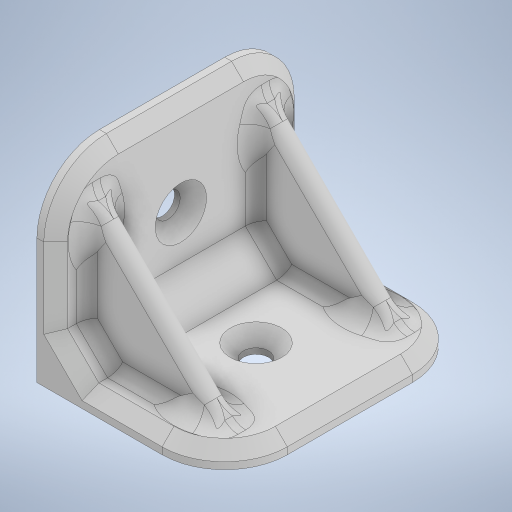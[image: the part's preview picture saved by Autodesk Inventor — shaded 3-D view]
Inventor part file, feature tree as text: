
AUTODESK INVENTOR PART (.ipt)
format: ipt  version: 2024.1 (Build 281209000, 209)  size: 785,920 bytes
history: native  units: in
note: dims shown in document units (in); Inventor stores cm internally (conversion verified against a paired STEP export)
features: sketch x7, extrude x5, fillet x4, plane x2, chamfer x2, hole x2, other x1, mirror x1, projected_geometry x1
ambient origin geometry x8: Origin, YZ Plane, XZ Plane, XY Plane, X Axis, Y Axis, Z Axis, Center Point
bodies: Body1 (feature_tree)
feature tree (25):
  other  "bracket"
  extrude  "Extrusion1"  Depth=1.1811in
  extrude  "Extrusion2"  Depth=0.1181in
  extrude  "Extrusion3"  Depth=0.1575in
  extrude  "Extrusion4"  Depth=0.7874in
  plane  "Work Plane1"
  extrude  "Extrusion5"  Depth=0.5906in
  plane  "Work Plane3"
  fillet  "Fillet1"  Radius=1.063in
  chamfer  "Chamfer1"  Distance=0.5906in
  fillet  "Fillet2"  Radius=1.5748in
  fillet  "Fillet3"  Radius=0.7874in
  chamfer  "Chamfer2"  Distance=1.063in
  sketch  "Sketch8"  dims[d16=0.1575in]
  sketch  "Sketch9"  dims[d17=1.1811in d18=0.5906in d19=1.5748in d20=0.7874in d21=1.063in d22=0.0in d27=-0.1969in d28=0.1969in d29=0.1969in d30=0.1181in d31=0.0in d32=0.3937in d33=0.1969in d34=0.0787in d35=45.0deg d36=0.0669in d37=0.0591in d38=0.0748in d39=0.0787in d40=45.0deg d41=0.1575in d42=0.2362in d43=0.3228in d44=0.0787in d45=90.0deg d46=0.315in d47=0.8108in d48=0.1575in d49=0.2362in d50=0.3228in d51=0.0787in d52=90.0deg d53=0.315in d54=0.8108in d55=0.1181in]
  hole  "Hole1"  [1 undecoded]
  hole  "Hole2"  [1 undecoded]
  fillet  "Fillet4"  Radius=0.1969in
  mirror  "Mirror1"
  sketch  "Sketch1"  dims[d0=1.5748in d1=1.1811in]
  sketch  "Sketch2"  dims[d2=0.1181in d3=0.0in d4=0.1181in]
  sketch  "Sketch3"  dims[d5=1.063in d6=0.0in d7=0.1575in]
  sketch  "Sketch4"  dims[d8=1.5748in d9=0.7874in]
  sketch  "Sketch7"  dims[d12=1.1811in d13=0.5906in d14=1.063in d15=0.0in]
  projected_geometry  "Projected Loop1"
note: 2 required parameter values undecoded (feature->parameter linkage not recoverable at this tier; creation-order binding heuristic only, values carry confidence <= 0.55)
